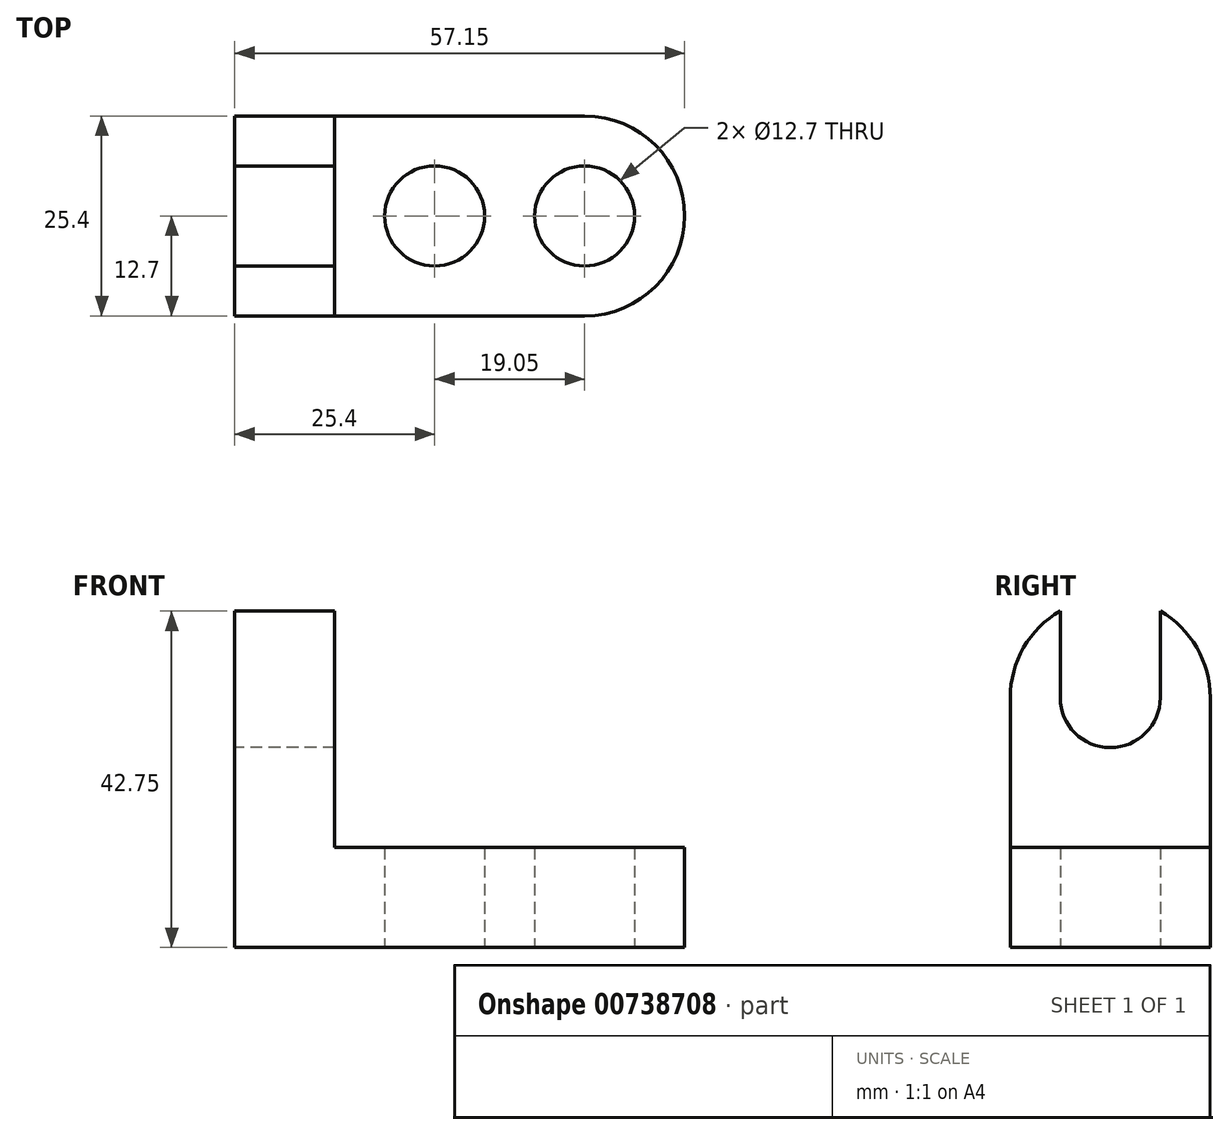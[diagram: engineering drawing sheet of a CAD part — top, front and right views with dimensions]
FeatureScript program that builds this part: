
annotation { "Feature Type Name" : "Feature", "Feature Type Description" : "" }
export const myFeature = defineFeature(function(context is Context, id is Id, definition is map)
    precondition{}
    {
        {
            var Q0;
            Q0=qCreatedBy(makeId("Front.planeOp"),FACE);
            var sketch = newSketch(context, id + "F0", { "sketchPlane" : qUnion([Q0])});
            skLineSegment(sketch, "E0", {"start": v(0, 44.45) * mm, "end": v(0, 0) * mm});
            skLineSegment(sketch, "E1", {"start": v(0, 0) * mm, "end": v(57.15, 0) * mm});
            skLineSegment(sketch, "E2", {"start": v(57.15, 0) * mm, "end": v(57.15, 12.7) * mm});
            skLineSegment(sketch, "E3", {"start": v(57.15, 12.7) * mm, "end": v(12.7, 12.7) * mm});
            skLineSegment(sketch, "E4", {"start": v(12.7, 12.7) * mm, "end": v(12.7, 44.45) * mm});
            skLineSegment(sketch, "E5", {"start": v(12.7, 44.45) * mm, "end": v(0, 44.45) * mm});
            skSolve(sketch);
        }
        {
            var Q0;
            Q0 = qSketchRegion(id + "F0", true);
            extrude(context, id + "F1", {"entities" : qUnion([Q0]), "depth" : 25.4 * mm, "offsetDistance" : 25.4 * mm});
        }
        {
            var Q0;
            Q0=qCreatedBy(makeId("Top.planeOp"),FACE);
            var sketch = newSketch(context, id + "F2", { "sketchPlane" : qUnion([Q0])});
            skCircle(sketch, "E6", {"center": v(44.45, -12.7) * mm, "radius": 6.35 * mm});
            skCircle(sketch, "E7", {"center": v(25.4, -12.7) * mm, "radius": 6.35 * mm});
            skSolve(sketch);
        }
        {
            var Q0;
            Q0 = qSketchRegion(id + "F2", true);
            extrude(context, id + "F3", {"entities" : qUnion([Q0]), "operationType" : NewBodyOperationType.REMOVE, "endBound" : BoundingType.THROUGH_ALL, "depth" : 25.4 * mm, "offsetDistance" : 25.4 * mm});
        }
        {
            var Q0;
            Q0=qCreatedBy(makeId("Right.planeOp"),FACE);
            var sketch = newSketch(context, id + "F4", { "sketchPlane" : qUnion([Q0])});
            skCircle(sketch, "E8", {"center": v(-12.7, 31.75) * mm, "radius": 6.35 * mm});
            skLineSegment(sketch, "E9", {"start": v(-6.35, 31.75) * mm, "end": v(-6.35, 44.45) * mm});
            skLineSegment(sketch, "E10", {"start": v(-6.35, 44.45) * mm, "end": v(-19.05, 44.45) * mm});
            skLineSegment(sketch, "E11", {"start": v(-19.05, 44.45) * mm, "end": v(-19.05, 31.75) * mm});
            skSolve(sketch);
        }
        {
            var Q0;
            Q0 = qSketchRegion(id + "F4", true);
            extrude(context, id + "F5", {"entities" : qUnion([Q0]), "operationType" : NewBodyOperationType.REMOVE, "endBound" : BoundingType.THROUGH_ALL, "depth" : 25.4 * mm, "offsetDistance" : 25.4 * mm});
        }
        {
            var Q0;
            Q0=qCreatedBy(makeId("Right.planeOp"),FACE);
            var sketch = newSketch(context, id + "F6", { "sketchPlane" : qUnion([Q0])});
            skArc(sketch, "E12", {"start": v(0, 31.75) * mm, "mid": v(-12.7, 44.45) * mm, "end": v(-25.4, 31.75) * mm});
            skLineSegment(sketch, "E13", {"start": v(-25.4, 31.75) * mm, "end": v(-25.4, 44.45) * mm});
            skLineSegment(sketch, "E14", {"start": v(-25.4, 44.45) * mm, "end": v(0, 44.45) * mm});
            skLineSegment(sketch, "E15", {"start": v(0, 44.45) * mm, "end": v(0, 31.75) * mm});
            skSolve(sketch);
        }
        {
            var Q0;
            Q0 = qSketchRegion(id + "F6", true);
            extrude(context, id + "F7", {"entities" : qUnion([Q0]), "operationType" : NewBodyOperationType.REMOVE, "endBound" : BoundingType.THROUGH_ALL, "depth" : 25.4 * mm, "offsetDistance" : 25.4 * mm});
        }
        {
            var Q0;
            Q0=qCreatedBy(makeId("Top.planeOp"),FACE);
            var sketch = newSketch(context, id + "F8", { "sketchPlane" : qUnion([Q0])});
            skArc(sketch, "E16", {"start": v(44.45, -25.4) * mm, "mid": v(57.15, -12.7) * mm, "end": v(44.45, 0) * mm});
            skLineSegment(sketch, "E17", {"start": v(44.45, 0) * mm, "end": v(57.15, 0) * mm});
            skLineSegment(sketch, "E18", {"start": v(57.15, 0) * mm, "end": v(57.15, -25.4) * mm});
            skLineSegment(sketch, "E19", {"start": v(57.15, -25.4) * mm, "end": v(44.45, -25.4) * mm});
            skSolve(sketch);
        }
        {
            var Q0;
            Q0 = qSketchRegion(id + "F8", true);
            extrude(context, id + "F9", {"entities" : qUnion([Q0]), "operationType" : NewBodyOperationType.REMOVE, "endBound" : BoundingType.THROUGH_ALL, "depth" : 25.4 * mm, "offsetDistance" : 25.4 * mm});
        }
    });
